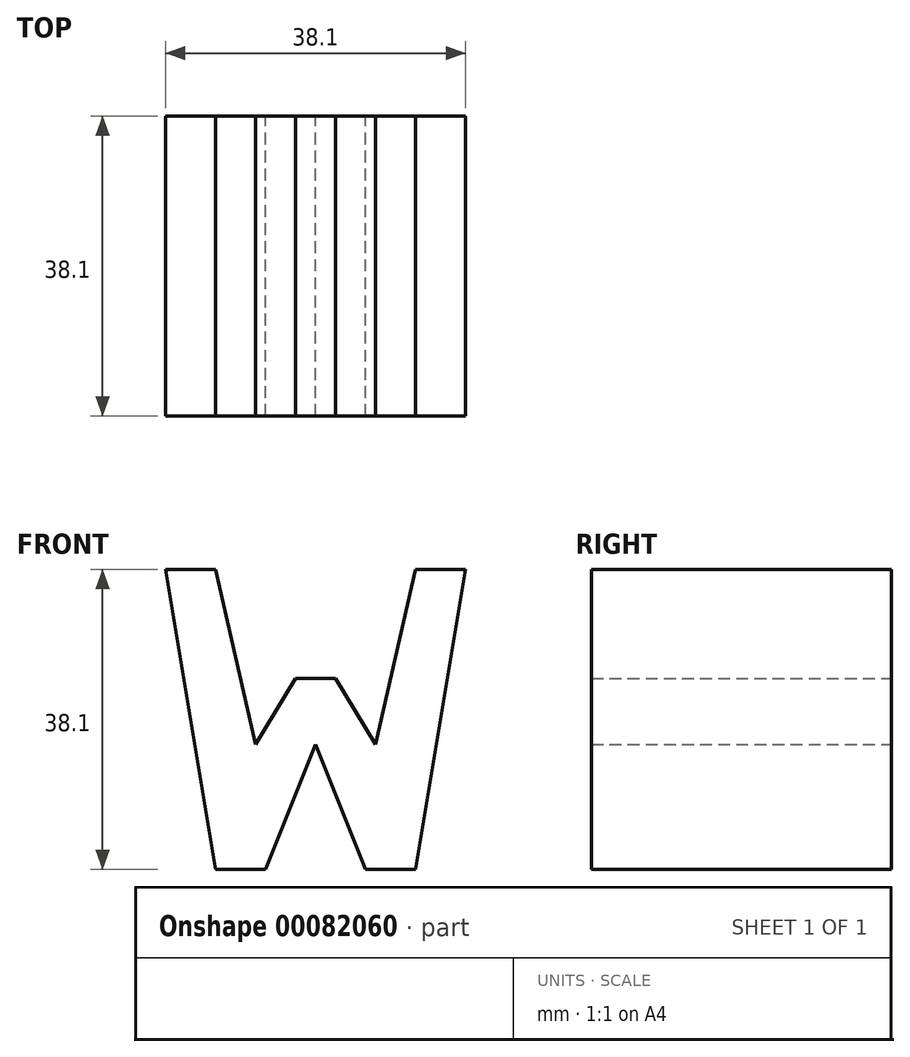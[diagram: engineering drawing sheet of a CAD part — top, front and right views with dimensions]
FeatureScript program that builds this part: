
annotation { "Feature Type Name" : "Feature", "Feature Type Description" : "" }
export const myFeature = defineFeature(function(context is Context, id is Id, definition is map)
    precondition{}
    {
        {
            var Q0;
            Q0=qCreatedBy(makeId("Front.planeOp"),FACE);
            var sketch = newSketch(context, id + "F0", { "sketchPlane" : qUnion([Q0])});
            skLineSegment(sketch, "E0", {"start": v(0, 0) * mm, "end": v(0, 38.1) * mm});
            skLineSegment(sketch, "E1", {"start": v(0, 38.1) * mm, "end": v(38.1, 38.1) * mm});
            skLineSegment(sketch, "E2", {"start": v(38.1, 38.1) * mm, "end": v(38.1, 0) * mm});
            skLineSegment(sketch, "E3", {"start": v(38.1, 0) * mm, "end": v(0, 0) * mm});
            skLineSegment(sketch, "E4", {"start": v(0, 38.1) * mm, "end": v(6.35, 0) * mm});
            skLineSegment(sketch, "E5", {"start": v(31.75, 0) * mm, "end": v(38.1, 38.1) * mm});
            skLineSegment(sketch, "E6", {"start": v(6.35, 38.1) * mm, "end": v(11.43, 15.88) * mm});
            skLineSegment(sketch, "E7", {"start": v(11.43, 15.88) * mm, "end": v(16.51, 24.24) * mm});
            skLineSegment(sketch, "E8", {"start": v(16.51, 24.24) * mm, "end": v(21.59, 24.24) * mm});
            skLineSegment(sketch, "E9", {"start": v(21.6, 24.24) * mm, "end": v(26.67, 15.88) * mm});
            skLineSegment(sketch, "E10", {"start": v(26.67, 15.88) * mm, "end": v(31.75, 38.1) * mm});
            skLineSegment(sketch, "E11", {"start": v(12.7, 0) * mm, "end": v(19.05, 15.88) * mm});
            skLineSegment(sketch, "E12", {"start": v(19.05, 15.88) * mm, "end": v(25.4, 0) * mm});
            skSolve(sketch);
        }
        {
            var Q0;
            Q0=qCreatedBy(makeId("Right.planeOp"),FACE);
            cPlane(context, id + "F1", {"entities" : qUnion([Q0]), "cplaneType" : CPlaneType.OFFSET, "offset" : 38.1 * mm, "width" : 152.4 * mm, "height" : 152.4 * mm});
        }
        {
            var Q0;
            Q0=qCreatedBy(id+"F1.planeOp",FACE);
            var sketch = newSketch(context, id + "F2", { "sketchPlane" : qUnion([Q0])});
            skLineSegment(sketch, "E13.bottom", {"start": v(0, 0) * mm, "end": v(-38.1, 0) * mm});
            skLineSegment(sketch, "E13.top", {"start": v(0, 38.1) * mm, "end": v(-38.1, 38.1) * mm});
            skLineSegment(sketch, "E13.left", {"start": v(0, 0) * mm, "end": v(0, 38.1) * mm});
            skLineSegment(sketch, "E13.right", {"start": v(-38.1, 0) * mm, "end": v(-38.1, 38.1) * mm});
            skSolve(sketch);
        }
        {
            var Q0;
            Q0 = qSketchRegion(id + "F2", true);
            extrude(context, id + "F3", {"entities" : qUnion([Q0]), "oppositeDirection" : true, "depth" : 38.1 * mm});
        }
        {
            var Q0;
            {var subQ0=sQuery(id+"F0.wireOp",EDGE,"E0");Q0=makeQuery(id+"F0.imprint","IMPRINT",FACE,{"disambiguationData":[TD([[makeQuery(id+"F0.imprint","IMPRINT",EDGE,{"derivedFrom":subQ0}),-1.0]])]});}
            var Q1;
            {var subQ0=sQuery(id+"F0.wireOp",EDGE,"E6");Q1=makeQuery(id+"F0.imprint","IMPRINT",FACE,{"disambiguationData":[TD([[makeQuery(id+"F0.imprint","IMPRINT",EDGE,{"derivedFrom":subQ0}),1.0]])]});}
            var Q2;
            {var subQ0=sQuery(id+"F0.wireOp",EDGE,"E2");Q2=makeQuery(id+"F0.imprint","IMPRINT",FACE,{"disambiguationData":[TD([[makeQuery(id+"F0.imprint","IMPRINT",EDGE,{"derivedFrom":subQ0}),-1.0]])]});}
            var Q3;
            {var subQ0=sQuery(id+"F0.wireOp",EDGE,"E11");Q3=makeQuery(id+"F0.imprint","IMPRINT",FACE,{"disambiguationData":[TD([[makeQuery(id+"F0.imprint","IMPRINT",EDGE,{"derivedFrom":subQ0}),-1.0]])]});}
            extrude(context, id + "F4", {"entities" : qUnion([Q0, Q1, Q2, Q3]), "operationType" : NewBodyOperationType.REMOVE, "depth" : 38.1 * mm});
        }
    });
